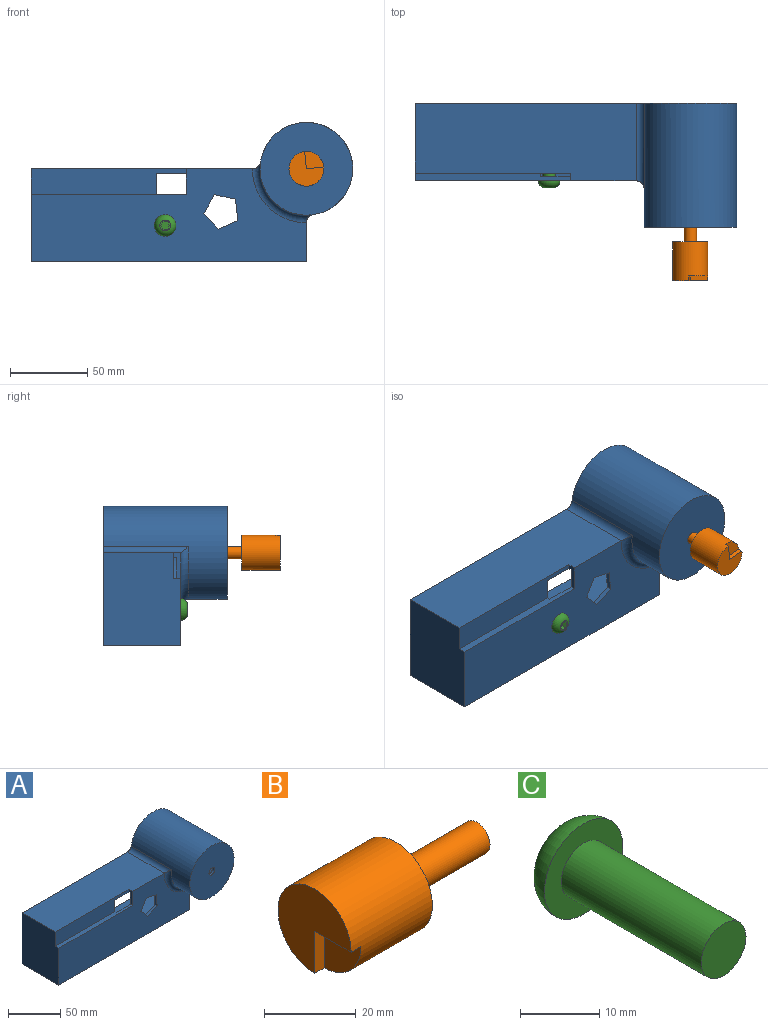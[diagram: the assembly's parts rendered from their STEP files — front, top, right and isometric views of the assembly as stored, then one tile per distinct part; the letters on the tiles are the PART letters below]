
ASSEMBLY  parts=3 mates=2
PART A: 27 faces, bbox 208x80x90 mm
  f0: plane 178x60mm, normal (0,-1,0), area 7726.4mm2, adj f2,f5,f6,f15,f19,f20,f21,f22
  f1: plane 94x54mm, normal (0,1,0), area 4061.9mm2, adj f3,f9,f10,f11,f12,f19,f20,f21
  f2: plane 143.36x50.01mm, normal (0,0,1), area 6666.1mm2, adj f0,f4,f15,f16,f18,f19,f26
  f3: plane 70.17x47mm, normal (0,0,-1), area 3259.1mm2, adj f1,f4,f10,f12,f18,f19
  f4: plane 208x90mm, normal (0,1,0), area 5862.7mm2, adj f2,f3,f5,f6,f7,f9,f10,f11
  f5: plane 50.01x25.36mm, normal (1,0,0), area 1268mm2, adj f0,f4,f6,f14,f15
  f6: plane 178x50mm, normal (0,0,-1), area 8900mm2, adj f0,f4,f5,f26
  f7: cylinder r=30mm len=80mm, axis (0,1,0), area 12014.8mm2, adj f4,f8,f14,f15,f16
  f8: plane 60x60mm, normal (0,-1,0), area 2777.2mm2, adj f7,f17
  f9: plane 47x30.17mm, normal (-1,0,0), area 1417.9mm2, adj f1,f4,f11,f12
  f10: plane 54x47mm, normal (1,0,0), area 2510.9mm2, adj f1,f3,f4,f11,f18,f20
  f11: plane 94x47mm, normal (0,0,1), area 4418mm2, adj f1,f4,f9,f10
  f12: cylinder r=27mm len=77mm, axis (0,1,0), area 11352mm2, adj f1,f3,f4,f9,f13
  f13: plane 54x54mm, normal (0,1,0), area 2240mm2, adj f12,f17
  f14: cylinder r=5mm len=55mm, axis (0,1,0), area 370.2mm2, adj f4,f5,f7,f15
  f15: torus R=35mm, axis (0,-1,0), area 416mm2, adj f0,f2,f5,f7,f14,f16
  f16: cylinder r=5mm len=55mm, axis (0,1,0), area 370.2mm2, adj f2,f4,f7,f15
  f17: cylinder r=4mm len=8mm, axis (0,-1,0), area 75.4mm2, adj f8,f13
  f18: plane 100.38x16.53mm, normal (0,-1,0), area 1397.4mm2, adj f2,f3,f10,f19,f20,f26
  f19: plane 16.53x5mm, normal (-1,0,0), area 55.6mm2, adj f0,f1,f2,f3,f18,f20
  f20: plane 100.38x5mm, normal (0,0,1), area 463.1mm2, adj f0,f1,f10,f18,f19,f26
  f21: plane 13.82x3mm, normal (-0.99,0,-0.1), area 41.7mm2, adj f0,f1,f22,f25
  f22: plane 13.58x3mm, normal (-0.21,0,-0.98), area 41.7mm2, adj f0,f1,f21,f23
  f23: plane 12.01x6.98mm, normal (0.86,0,-0.5), area 41.7mm2, adj f0,f1,f22,f24
  f24: plane 10.35x9.26mm, normal (0.75,0,0.67), area 41.7mm2, adj f0,f1,f23,f25
  f25: plane 12.7x5.61mm, normal (-0.4,0,0.91), area 41.7mm2, adj f0,f1,f21,f24
  f26: plane 60x50mm, normal (-1,0,0), area 2917.3mm2, adj f0,f2,f4,f6,f18,f20
PART B: 8 faces, bbox 50x22.5x22.5 mm
  f0: plane 22.52x22.52mm, normal (-1,0,0), area 298.7mm2, adj f3,f5,f6
  f1: cylinder r=4mm len=25mm, axis (-1,0,0), area 628.3mm2, adj f2,f4
  f2: plane 8x8mm, normal (1,0,0), area 50.3mm2, adj f1
  f3: cylinder r=11.26mm len=25mm, axis (1,0,0), area 1715.7mm2, adj f0,f4,f5,f6,f7
  f4: plane 22.52x22.52mm, normal (1,0,0), area 348mm2, adj f1,f3
  f5: plane 11.26x3mm, normal (0,0,-1), area 33.8mm2, adj f0,f3,f6,f7
  f6: plane 11.26x3mm, normal (0,-1,0), area 33.8mm2, adj f0,f3,f5,f7
  f7: plane 11.26x11.26mm, normal (-1,0,0), area 99.6mm2, adj f3,f5,f6
PART C: 12 faces, bbox 14x29.4x14 mm
  f0: plane 7x7mm, normal (0,1,0), area 16.8mm2, adj f3,f5,f6,f7,f8,f9,f10
  f1: cylinder r=4mm len=25mm, axis (0,1,0), area 628.3mm2, adj f2,f4
  f2: plane 8x8mm, normal (0,-1,0), area 50.3mm2, adj f1
  f3: torus R=2.48mm, axis (0,1,0), area 219.6mm2, adj f0,f4
  f4: plane 14x14mm, normal (0,-1,0), area 103.7mm2, adj f1,f3
  f5: plane 4x2.5mm, normal (-0.5,0,0.87), area 11.5mm2, adj f0,f6,f10,f11
  f6: plane 4x2.5mm, normal (0.5,0,0.87), area 11.5mm2, adj f0,f5,f7,f11
  f7: plane 4x2.89mm, normal (1,0,0), area 11.5mm2, adj f0,f6,f8,f11
  f8: plane 4x2.5mm, normal (0.5,0,-0.87), area 11.5mm2, adj f0,f7,f9,f11
  f9: plane 4x2.5mm, normal (-0.5,0,-0.87), area 11.5mm2, adj f0,f8,f10,f11
  f10: plane 4x2.89mm, normal (-1,0,0), area 11.5mm2, adj f0,f5,f9,f11
  f11: plane 5.77x5mm, normal (0,1,0), area 21.7mm2, adj f5,f6,f7,f8,f9,f10
PLACE A t=(-62.46,9.64,-59.61)mm fixed
PLACE B rot(axis=(-0.6,-0.6,0.54),123.5deg) t=(-5.13,-79.86,-4.1)mm
PLACE C rot(axis=(0.71,0,0.71),180deg) t=(-53.84,-40.36,-36.26)mm
MATE revolute B.f1 <-> A.f7  axis (0,-1,0) through (37.54,-67.36,0.39)mm
MATE fastened C.f1 <-> A.f0  axis (0,-1,0) through (-53.84,-40.36,-36.26)mm
